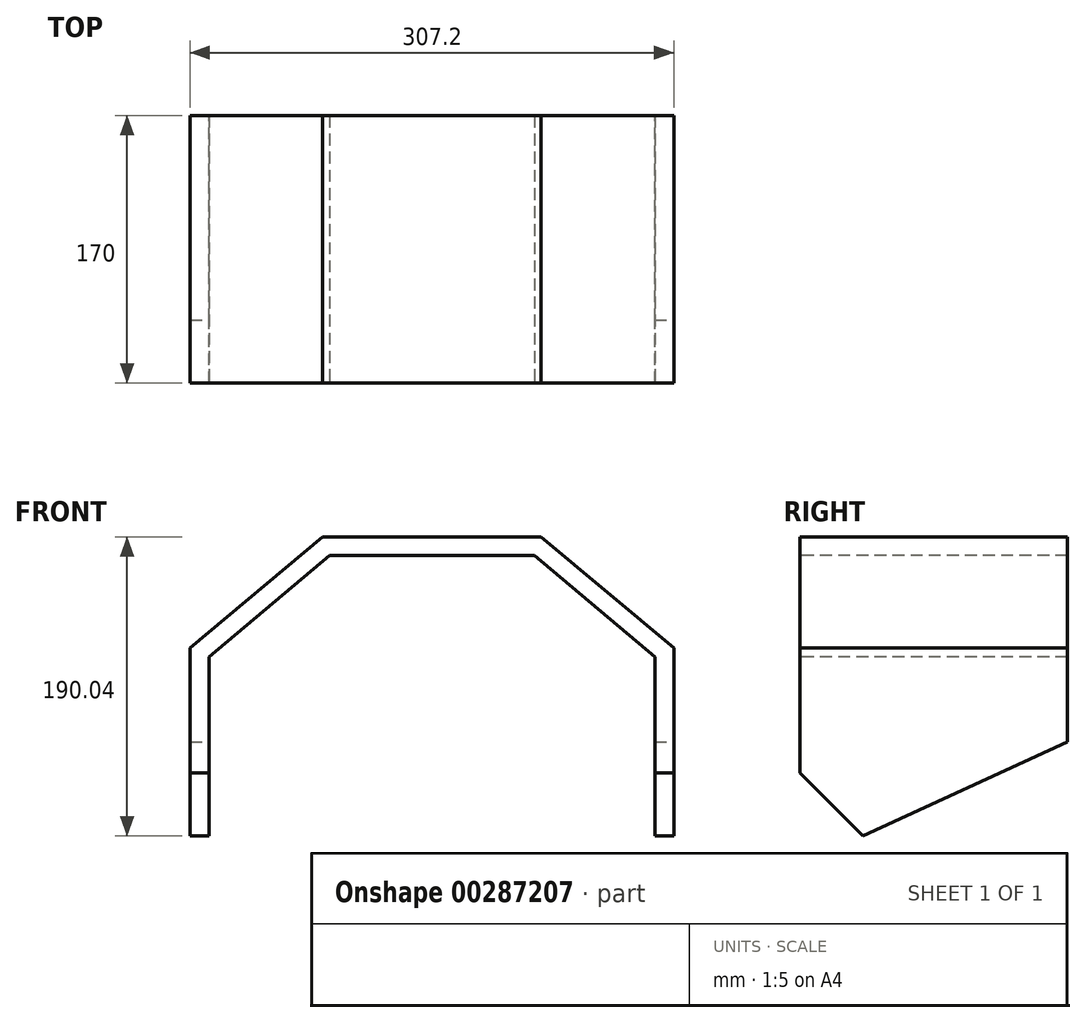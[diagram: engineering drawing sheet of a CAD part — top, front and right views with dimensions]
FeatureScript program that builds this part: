
annotation { "Feature Type Name" : "Feature", "Feature Type Description" : "" }
export const myFeature = defineFeature(function(context is Context, id is Id, definition is map)
    precondition{}
    {
        {
            var Q0;
            Q0=qCreatedBy(makeId("Front.planeOp"),FACE);
            var sketch = newSketch(context, id + "F0", { "sketchPlane" : qUnion([Q0])});
            skLineSegment(sketch, "E0", {"start": v(-65, 83.02) * mm, "end": v(65, 83.02) * mm});
            skLineSegment(sketch, "E1", {"start": v(-69.37, 95.02) * mm, "end": v(69.37, 95.02) * mm});
            skLineSegment(sketch, "E2", {"start": v(65, 83.02) * mm, "end": v(141.6, 18.75) * mm});
            skLineSegment(sketch, "E3", {"start": v(69.37, 95.02) * mm, "end": v(153.6, 24.34) * mm});
            skLineSegment(sketch, "E4", {"start": v(141.6, 18.75) * mm, "end": v(141.6, -95.02) * mm});
            skLineSegment(sketch, "E5", {"start": v(153.6, 24.34) * mm, "end": v(153.6, -95.02) * mm});
            skLineSegment(sketch, "E6", {"start": v(-65, 83.02) * mm, "end": v(-141.6, 18.75) * mm});
            skLineSegment(sketch, "E7", {"start": v(-69.37, 95.02) * mm, "end": v(-153.6, 24.34) * mm});
            skLineSegment(sketch, "E8", {"start": v(-141.6, 18.75) * mm, "end": v(-141.6, -95.02) * mm});
            skLineSegment(sketch, "E9", {"start": v(-153.6, 24.34) * mm, "end": v(-153.6, -95.02) * mm});
            skLineSegment(sketch, "E10", {"start": v(153.6, -95.02) * mm, "end": v(141.6, -95.02) * mm});
            skLineSegment(sketch, "E11", {"start": v(-141.6, -95.02) * mm, "end": v(-153.6, -95.02) * mm});
            skSolve(sketch);
        }
        {
            var Q0;
            Q0 = qSketchRegion(id + "F0", true);
            extrude(context, id + "F1", {"entities" : qUnion([Q0]), "oppositeDirection" : true, "depth" : 170 * mm});
        }
        {
            var Q0;
            Q0=makeQuery(id+"F1.opExtrude","SWEPT_FACE",FACE,{"disambiguationData":[OSD([sQuery(id+"F0.wireOp",EDGE,"E5")])]});
            var sketch = newSketch(context, id + "F2", { "sketchPlane" : qUnion([Q0])});
            skLineSegment(sketch, "E12", {"start": v(40, -110.76) * mm, "end": v(40, -95.02) * mm});
            skLineSegment(sketch, "E13", {"start": v(170, -35.34) * mm, "end": v(40, -95.02) * mm});
            skLineSegment(sketch, "E14", {"start": v(40, -110.76) * mm, "end": v(189.8, -110.76) * mm});
            skLineSegment(sketch, "E15", {"start": v(189.8, -110.76) * mm, "end": v(189.8, -35.34) * mm});
            skLineSegment(sketch, "E16", {"start": v(189.8, -35.34) * mm, "end": v(170, -35.34) * mm});
            skSolve(sketch);
        }
        {
            var Q0;
            {var subQ0=sQuery(id+"F2.wireOp",EDGE,"E13");Q0=makeQuery(id+"F2.imprint","IMPRINT",FACE,{"disambiguationData":[TD([[makeQuery(id+"F2.imprint","IMPRINT",EDGE,{"derivedFrom":subQ0}),1.0]])]});}
            extrude(context, id + "F3", {"entities" : qUnion([Q0]), "operationType" : NewBodyOperationType.REMOVE, "oppositeDirection" : true, "depth" : 350 * mm});
        }
        {
            var Q0;
            Q0=makeQuery(id+"F1.opExtrude","SWEPT_FACE",FACE,{"disambiguationData":[OSD([sQuery(id+"F0.wireOp",EDGE,"E5")])]});
            var sketch = newSketch(context, id + "F4", { "sketchPlane" : qUnion([Q0])});
            skLineSegment(sketch, "E17", {"start": v(40, -95.02) * mm, "end": v(0, -55.02) * mm});
            skLineSegment(sketch, "E18", {"start": v(0, -55.02) * mm, "end": v(0, -95.02) * mm});
            skLineSegment(sketch, "E19", {"start": v(0, -95.02) * mm, "end": v(40, -95.02) * mm});
            skSolve(sketch);
        }
        {
            var Q0;
            Q0=makeQuery(id+"F4.imprint","IMPRINT",FACE,{"disambiguationData":[TD([[makeQuery(id+"F4.imprint","IMPRINT",EDGE,{"derivedFrom":sQuery(id+"F4.wireOp",EDGE,"E17")}),1.0]])]});
            extrude(context, id + "F5", {"entities" : qUnion([Q0]), "operationType" : NewBodyOperationType.REMOVE, "oppositeDirection" : true, "depth" : 400 * mm});
        }
    });
